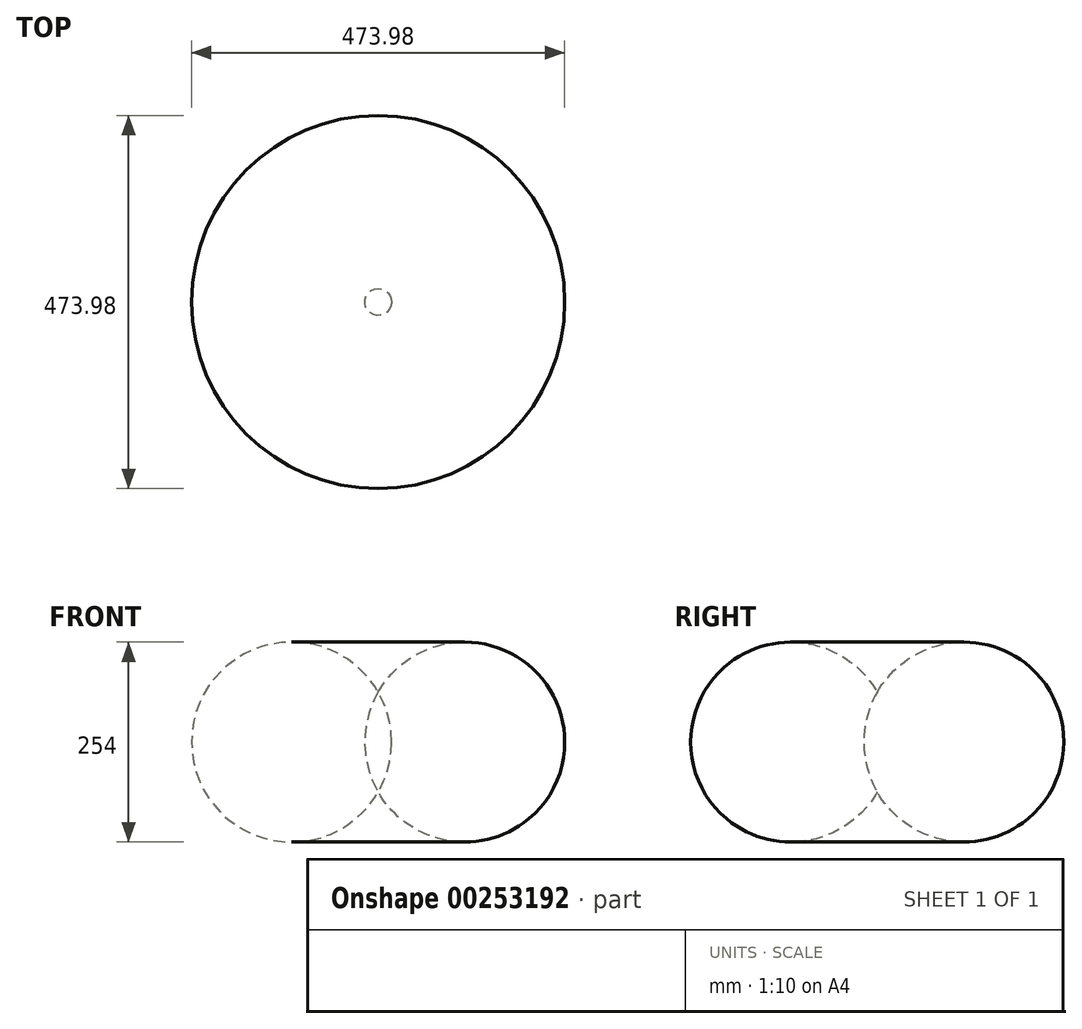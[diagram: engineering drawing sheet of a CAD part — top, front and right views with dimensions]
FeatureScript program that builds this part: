
annotation { "Feature Type Name" : "Feature", "Feature Type Description" : "" }
export const myFeature = defineFeature(function(context is Context, id is Id, definition is map)
    precondition{}
    {
        {
            var Q0;
            Q0=qCreatedBy(makeId("Front.planeOp"),FACE);
            var sketch = newSketch(context, id + "F0", { "sketchPlane" : qUnion([Q0])});
            skLineSegment(sketch, "E0", {"start": v(0, 0) * mm, "end": v(0, 127) * mm});
            skArc(sketch, "E1", {"start": v(0, 0) * mm, "mid": v(17.01, 63.5) * mm, "end": v(0, 127) * mm});
            skSolve(sketch);
        }
        {
            var Q0;
            Q0=makeQuery(id+"F0.imprint","IMPRINT",FACE,{"disambiguationData":[TD([[makeQuery(id+"F0.imprint","IMPRINT",EDGE,{"derivedFrom":sQuery(id+"F0.wireOp",EDGE,"E0")}),-1.0]])]});
            var Q1;
            Q1=sQuery(id+"F0.wireOp",EDGE,"E0");
            revolve(context, id + "F1", {"entities" : qUnion([Q0]), "axis" : qUnion([Q1]), "revolveType" : RevolveType.FULL});
        }
    });
